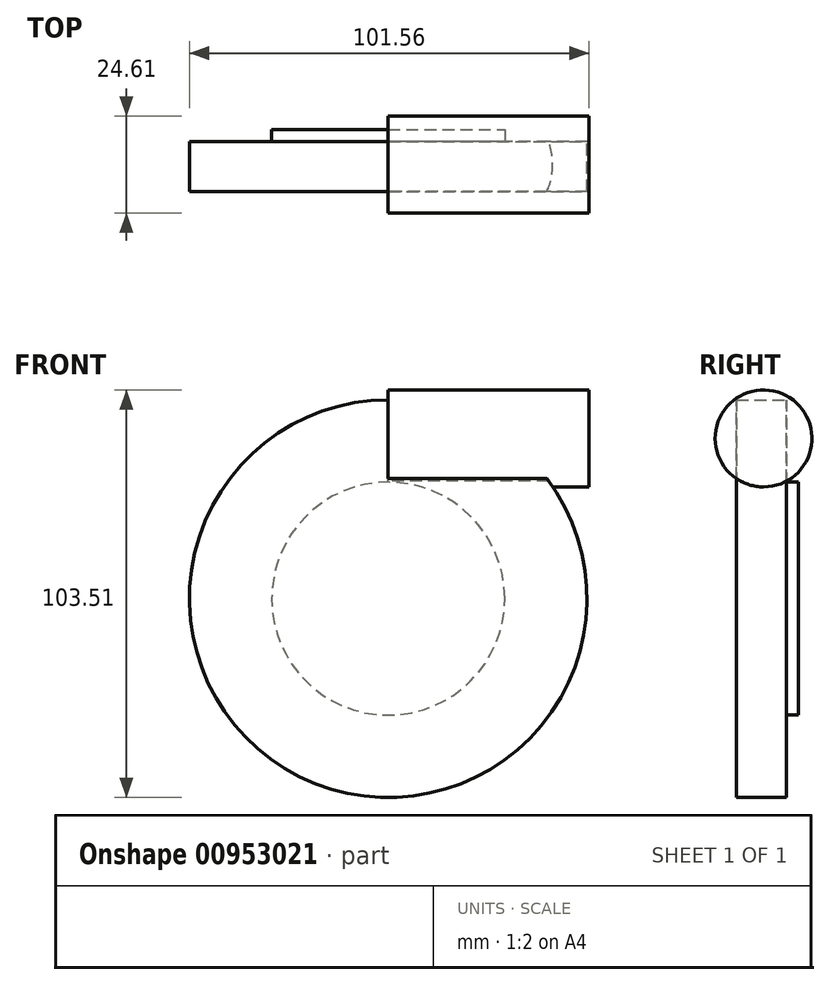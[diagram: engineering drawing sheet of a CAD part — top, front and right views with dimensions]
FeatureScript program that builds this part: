
annotation { "Feature Type Name" : "Feature", "Feature Type Description" : "" }
export const myFeature = defineFeature(function(context is Context, id is Id, definition is map)
    precondition{}
    {
        {
            var Q0;
            Q0=qCreatedBy(makeId("Front.planeOp"),FACE);
            var sketch = newSketch(context, id + "F0", { "sketchPlane" : qUnion([Q0])});
            skCircle(sketch, "E0", {"center": v(0, 0) * mm, "radius": 50.51 * mm});
            skSolve(sketch);
        }
        {
            var Q0;
            Q0=makeQuery(id+"F0.imprint","IMPRINT",FACE,{"disambiguationData":[TD([[makeQuery(id+"F0.imprint","IMPRINT",EDGE,{"derivedFrom":sQuery(id+"F0.wireOp",EDGE,"E0")}),1.0]])]});
            extrude(context, id + "F1", {"entities" : qUnion([Q0]), "depth" : 12.7 * mm, "offsetDistance" : 25.4 * mm});
        }
        {
            var Q0;
            Q0=qCreatedBy(makeId("Right.planeOp"),FACE);
            var sketch = newSketch(context, id + "F2", { "sketchPlane" : qUnion([Q0])});
            skCircle(sketch, "E1", {"center": v(-5.81, 40.7) * mm, "radius": 12.3 * mm});
            skSolve(sketch);
        }
        {
            var Q0;
            Q0 = qSketchRegion(id + "F2", true);
            extrude(context, id + "F3", {"entities" : qUnion([Q0]), "operationType" : NewBodyOperationType.ADD, "depth" : 51.05 * mm, "offsetDistance" : 25.4 * mm});
        }
        {
            var Q0;
            Q0=qCreatedBy(makeId("Front.planeOp"),FACE);
            var sketch = newSketch(context, id + "F4", { "sketchPlane" : qUnion([Q0])});
            skCircle(sketch, "E2", {"center": v(0, 0) * mm, "radius": 29.6 * mm});
            skSolve(sketch);
        }
        {
            var Q0;
            Q0=makeQuery(id+"F4.imprint","IMPRINT",FACE,{"disambiguationData":[TD([[makeQuery(id+"F4.imprint","IMPRINT",EDGE,{"derivedFrom":sQuery(id+"F4.wireOp",EDGE,"E2")}),1.0]])]});
            extrude(context, id + "F5", {"entities" : qUnion([Q0]), "operationType" : NewBodyOperationType.ADD, "oppositeDirection" : true, "depth" : 3.05 * mm, "offsetDistance" : 25.4 * mm});
        }
    });
